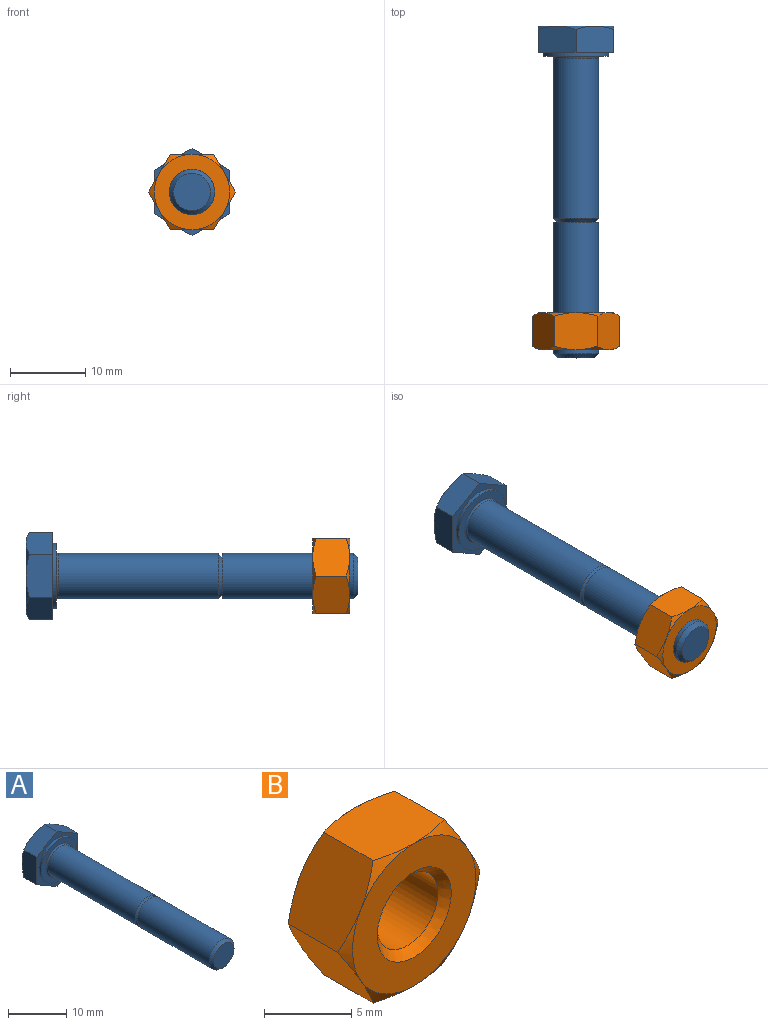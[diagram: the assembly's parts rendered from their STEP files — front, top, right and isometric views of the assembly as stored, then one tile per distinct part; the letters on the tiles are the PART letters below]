
ASSEMBLY  parts=2 mates=1
PART A: 23 faces, bbox 12x44.5x12 mm
  f0: plane 4.92x4.92mm, normal (0,-1,0), area 19mm2, adj f1
  f1: cone r=2.46mm half-angle=45deg, axis (0,1,0), area 13.1mm2, adj f0,f2
  f2: cylinder r=3mm len=17.46mm, axis (0,1,0), area 329.1mm2, adj f1,f3
  f3: plane 6x6mm, normal (0,1,0), area 9.3mm2, adj f2,f4
  f4: cone r=2.46mm half-angle=45deg, axis (0,1,0), area 13.1mm2, adj f3,f5
  f5: cylinder r=3mm len=21.21mm, axis (0,1,0), area 399.8mm2, adj f4,f6
  f6: torus R=3.25mm, axis (0,1,0), area 7.6mm2, adj f5,f7
  f7: plane 8.7x8.7mm, normal (0,-1,0), area 26.3mm2, adj f6,f8
  f8: cylinder r=4.35mm len=8.7mm, axis (0,1,0), area 13.7mm2, adj f7,f9
  f9: plane 11.55x10mm, normal (0,-1,0), area 27.2mm2, adj f8,f17,f18,f19,f20,f21,f22
  f10: cone r=5.77mm half-angle=60deg, axis (0,-1,0), area 2.5mm2, adj f15,f17,f18
  f11: cone r=5.77mm half-angle=60deg, axis (0,-1,0), area 2.5mm2, adj f15,f21,f22
  f12: cone r=5.77mm half-angle=60deg, axis (0,-1,0), area 2.5mm2, adj f15,f20,f21
  f13: cone r=5.77mm half-angle=60deg, axis (0,-1,0), area 2.5mm2, adj f15,f19,f20
  f14: cone r=5.77mm half-angle=60deg, axis (0,-1,0), area 2.5mm2, adj f15,f18,f19
  f15: plane 10x10mm, normal (0,1,0), area 78.5mm2, adj f10,f11,f12,f13,f14,f16
  f16: cone r=5.77mm half-angle=60deg, axis (0,-1,0), area 2.5mm2, adj f15,f17,f22
  f17: plane 5.47x3.98mm, normal (0.5,0,-0.87), area 19.3mm2, adj f9,f10,f16,f18,f22
  f18: plane 5.47x3.98mm, normal (-0.5,0,-0.87), area 19.3mm2, adj f9,f10,f14,f17,f19
  f19: plane 6.25x3.98mm, normal (-1,0,0), area 19.3mm2, adj f9,f13,f14,f18,f20
  f20: plane 5.47x3.98mm, normal (-0.5,0,0.87), area 19.3mm2, adj f9,f12,f13,f19,f21
  f21: plane 5.47x3.98mm, normal (0.5,0,0.87), area 19.3mm2, adj f9,f11,f12,f20,f22
  f22: plane 6.25x3.98mm, normal (1,0,0), area 19.3mm2, adj f9,f11,f16,f17,f21
PART B: 23 faces, bbox 12x5.4x12 mm
  f0: cone r=5mm half-angle=60deg, axis (0,-1,0), area 2.5mm2, adj f1,f21,f22
  f1: plane 10x10mm, normal (0,1,0), area 50.3mm2, adj f0,f2,f3,f4,f5,f6,f9
  f2: cone r=5mm half-angle=60deg, axis (0,-1,0), area 2.5mm2, adj f1,f20,f21
  f3: cone r=5mm half-angle=60deg, axis (0,-1,0), area 2.5mm2, adj f1,f19,f20
  f4: cone r=5mm half-angle=60deg, axis (0,-1,0), area 2.5mm2, adj f1,f18,f19
  f5: cone r=5mm half-angle=60deg, axis (0,-1,0), area 2.5mm2, adj f1,f17,f18
  f6: cone r=5mm half-angle=60deg, axis (0,-1,0), area 2.5mm2, adj f1,f17,f22
  f7: cone r=3mm half-angle=45deg, axis (0,-1,0), area 13.1mm2, adj f8,f10
  f8: cylinder r=2.46mm len=4.92mm, axis (0,1,0), area 59mm2, adj f7,f9
  f9: cone r=2.46mm half-angle=45deg, axis (0,1,0), area 13.1mm2, adj f1,f8
  f10: plane 10x10mm, normal (0,-1,0), area 50.3mm2, adj f7,f11,f12,f13,f14,f15,f16
  f11: cone r=5.77mm half-angle=60deg, axis (0,1,0), area 2.5mm2, adj f10,f21,f22
  f12: cone r=5.77mm half-angle=60deg, axis (0,1,0), area 2.5mm2, adj f10,f20,f21
  f13: cone r=5.77mm half-angle=60deg, axis (0,1,0), area 2.5mm2, adj f10,f19,f20
  f14: cone r=5.77mm half-angle=60deg, axis (0,1,0), area 2.5mm2, adj f10,f18,f19
  f15: cone r=5.77mm half-angle=60deg, axis (0,1,0), area 2.5mm2, adj f10,f17,f18
  f16: cone r=5.77mm half-angle=60deg, axis (0,1,0), area 2.5mm2, adj f10,f17,f22
  f17: plane 5.47x5.38mm, normal (0.87,0,-0.5), area 26.5mm2, adj f5,f6,f15,f16,f18,f22
  f18: plane 5.47x5.38mm, normal (0.87,0,0.5), area 26.5mm2, adj f4,f5,f14,f15,f17,f19
  f19: plane 6.25x5.38mm, normal (0,0,1), area 26.5mm2, adj f3,f4,f13,f14,f18,f20
  f20: plane 5.47x5.38mm, normal (-0.87,0,0.5), area 26.5mm2, adj f2,f3,f12,f13,f19,f21
  f21: plane 5.47x5.38mm, normal (-0.87,0,-0.5), area 26.5mm2, adj f0,f2,f11,f12,f20,f22
  f22: plane 6.25x5.38mm, normal (0,0,-1), area 26.5mm2, adj f0,f6,f11,f16,f17,f21
PLACE A t=(-11.32,7.09,-6.56)mm
PLACE B t=(-11.32,-26.91,-6.56)mm
MATE fastened B.f0 <-> A.f4  axis (0,1,0) through (-11.32,-26.91,-6.56)mm
